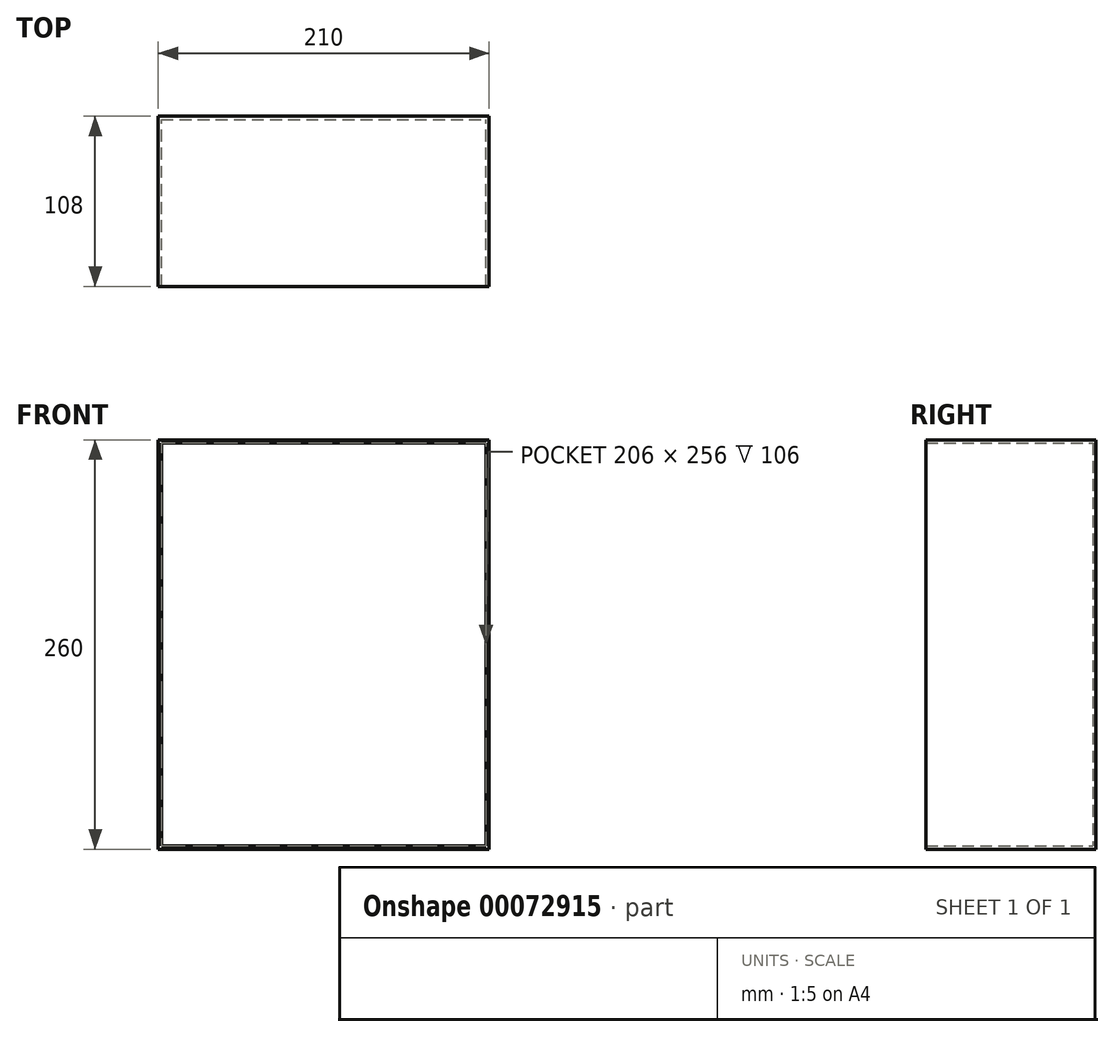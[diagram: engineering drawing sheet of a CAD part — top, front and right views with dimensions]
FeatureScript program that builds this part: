
annotation { "Feature Type Name" : "Feature", "Feature Type Description" : "" }
export const myFeature = defineFeature(function(context is Context, id is Id, definition is map)
    precondition{}
    {
        {
            var Q0;
            Q0=qCreatedBy(makeId("Front.planeOp"),FACE);
            var sketch = newSketch(context, id + "F0", { "sketchPlane" : qUnion([Q0])});
            skLineSegment(sketch, "E0.rect.bottom", {"start": v(-105, 130) * mm, "end": v(105, 130) * mm});
            skLineSegment(sketch, "E0.rect.top", {"start": v(-105, -130) * mm, "end": v(105, -130) * mm});
            skLineSegment(sketch, "E0.rect.left", {"start": v(-105, 130) * mm, "end": v(-105, -130) * mm});
            skLineSegment(sketch, "E0.rect.right", {"start": v(105, 130) * mm, "end": v(105, -130) * mm});
            skPoint(sketch, "E0.rect.middle", {"position": v(0, 0) * mm});
            skSolve(sketch);
        }
        {
            var Q0;
            Q0=makeQuery(id+"F0.imprint","IMPRINT",FACE,{"disambiguationData":[TD([[makeQuery(id+"F0.imprint","IMPRINT",EDGE,{"derivedFrom":sQuery(id+"F0.wireOp",EDGE,"E0.rect.bottom")}),-1.0]])]});
            extrude(context, id + "F1", {"entities" : qUnion([Q0]), "endBound" : BoundingType.SYMMETRIC, "depth" : 108 * mm});
        }
        {
            var Q0;
            Q0=makeQuery(id+"F1.opExtrude","CAP_FACE",FACE,{"disambiguationData":[OSD([sQuery(id+"F0.wireOp",EDGE,"E0.rect.bottom"),sQuery(id+"F0.wireOp",EDGE,"E0.rect.top"),sQuery(id+"F0.wireOp",EDGE,"E0.rect.left"),sQuery(id+"F0.wireOp",EDGE,"E0.rect.right")])],"isStart":false});
            shell(context, id + "F2", {"entities" : qUnion([Q0]), "thickness" : 2 * mm});
        }
    });
